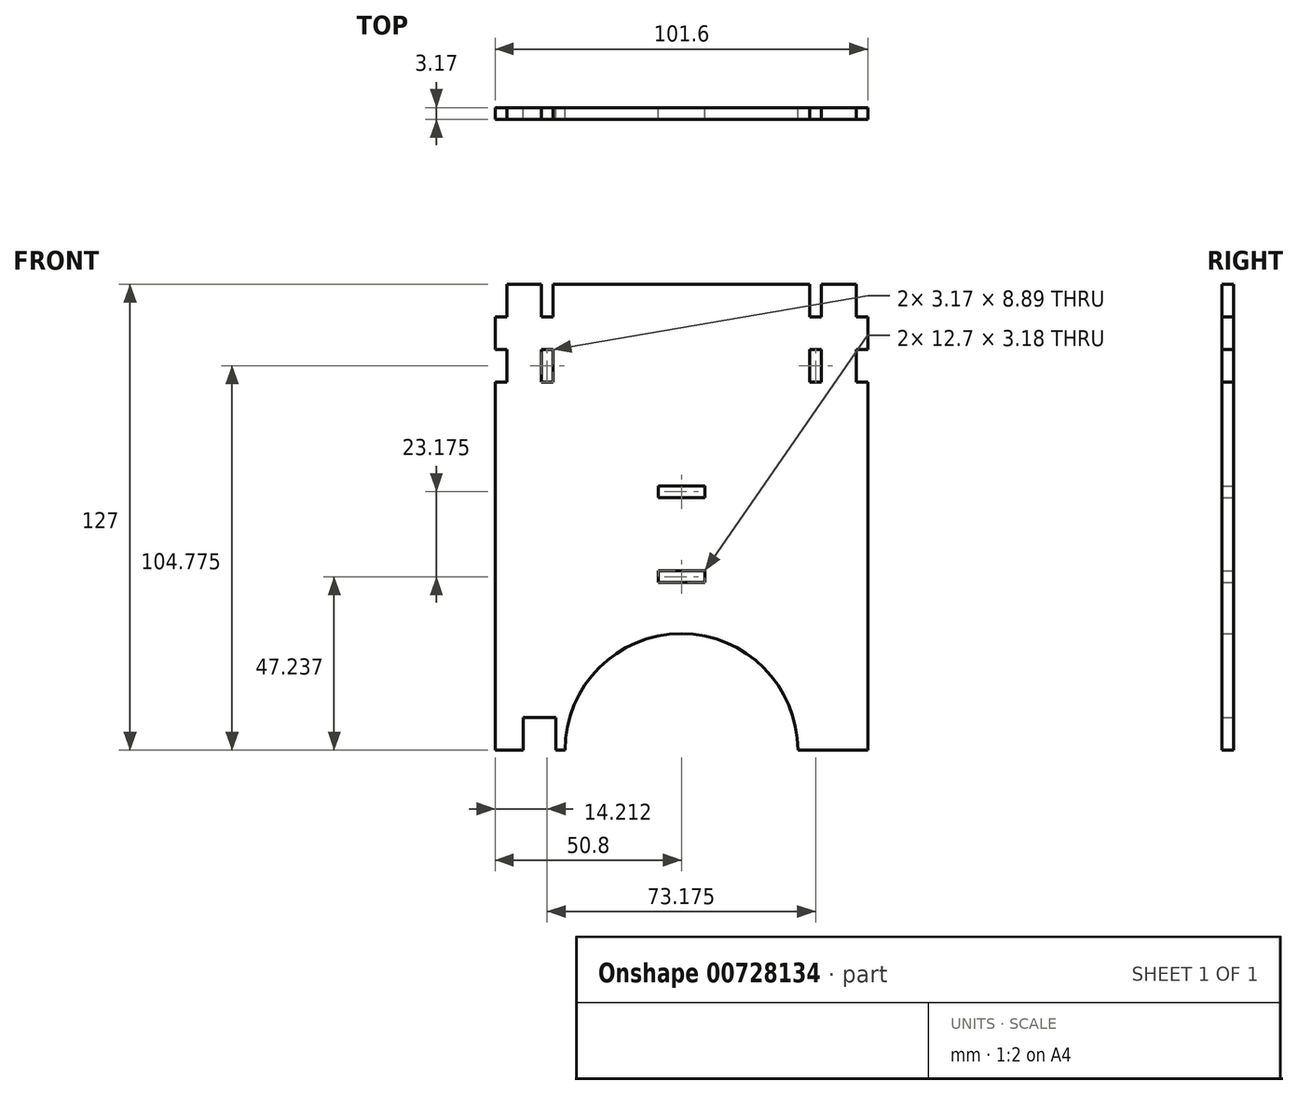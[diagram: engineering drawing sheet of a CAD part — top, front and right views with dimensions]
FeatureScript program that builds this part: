
annotation { "Feature Type Name" : "Feature", "Feature Type Description" : "" }
export const myFeature = defineFeature(function(context is Context, id is Id, definition is map)
    precondition{}
    {
        {
            var Q0;
            Q0=qCreatedBy(makeId("Front.planeOp"),FACE);
            var sketch = newSketch(context, id + "F0", { "sketchPlane" : qUnion([Q0])});
            skLineSegment(sketch, "E0.bottom", {"start": v(-50.8, 76.2) * mm, "end": v(50.8, 76.2) * mm});
            skLineSegment(sketch, "E0.top", {"start": v(-50.8, -76.2) * mm, "end": v(50.8, -76.2) * mm});
            skLineSegment(sketch, "E0.left", {"start": v(-50.8, 76.2) * mm, "end": v(-50.8, -76.2) * mm});
            skLineSegment(sketch, "E0.right", {"start": v(50.8, 76.2) * mm, "end": v(50.8, -76.2) * mm});
            skPoint(sketch, "E1", {"position": v(50.8, 0) * mm});
            skLineSegment(sketch, "E2", {"start": v(-47.62, 0) * mm, "end": v(-47.63, 76.2) * mm});
            skLineSegment(sketch, "E3", {"start": v(-50.8, 67.3) * mm, "end": v(-47.63, 67.3) * mm});
            skLineSegment(sketch, "E4", {"start": v(-50.8, 58.42) * mm, "end": v(-47.63, 58.42) * mm});
            skLineSegment(sketch, "E5", {"start": v(-50.8, 49.53) * mm, "end": v(-47.63, 49.53) * mm});
            skLineSegment(sketch, "E6", {"start": v(-50.8, 40.64) * mm, "end": v(-47.63, 40.64) * mm});
            skLineSegment(sketch, "E7", {"start": v(-50.8, 27.94) * mm, "end": v(-47.62, 27.94) * mm});
            skLineSegment(sketch, "E8", {"start": v(-47.62, 0) * mm, "end": v(-50.8, 0) * mm});
            skLineSegment(sketch, "E9", {"start": v(47.63, 76.2) * mm, "end": v(47.63, 0) * mm});
            skLineSegment(sketch, "E10", {"start": v(47.62, 67.31) * mm, "end": v(50.8, 67.31) * mm});
            skLineSegment(sketch, "E11", {"start": v(47.62, 58.42) * mm, "end": v(50.8, 58.42) * mm});
            skLineSegment(sketch, "E12", {"start": v(47.63, 38.1) * mm, "end": v(50.8, 38.1) * mm});
            skLineSegment(sketch, "E13", {"start": v(47.63, 25.4) * mm, "end": v(50.8, 25.4) * mm});
            skLineSegment(sketch, "E14", {"start": v(47.63, 12.7) * mm, "end": v(50.8, 12.7) * mm});
            skLineSegment(sketch, "E15", {"start": v(-35, 76.2) * mm, "end": v(-35, 0) * mm});
            skLineSegment(sketch, "E16", {"start": v(35, 76.2) * mm, "end": v(35, 0) * mm});
            skLineSegment(sketch, "E17", {"start": v(38.17, 0) * mm, "end": v(38.17, 76.2) * mm});
            skLineSegment(sketch, "E18", {"start": v(-38.18, 76.2) * mm, "end": v(-38.18, 0) * mm});
            skLineSegment(sketch, "E19", {"start": v(-38.17, 67.3) * mm, "end": v(-35, 67.3) * mm});
            skLineSegment(sketch, "E20", {"start": v(-35, -59.7) * mm, "end": v(-38.17, -59.7) * mm});
            skLineSegment(sketch, "E21", {"start": v(-35, -72.4) * mm, "end": v(-38.17, -72.4) * mm});
            skLineSegment(sketch, "E22", {"start": v(-38.17, -85.1) * mm, "end": v(-35, -85.1) * mm});
            skLineSegment(sketch, "E23", {"start": v(-35, -97.8) * mm, "end": v(-38.17, -97.8) * mm});
            skLineSegment(sketch, "E24", {"start": v(-38.18, 0) * mm, "end": v(-35, 0) * mm});
            skLineSegment(sketch, "E25", {"start": v(35, 0) * mm, "end": v(38.17, 0) * mm});
            skLineSegment(sketch, "E26", {"start": v(38.18, 27.94) * mm, "end": v(35, 27.94) * mm});
            skLineSegment(sketch, "E27", {"start": v(35, 40.64) * mm, "end": v(38.18, 40.64) * mm});
            skLineSegment(sketch, "E28", {"start": v(35, 49.53) * mm, "end": v(38.18, 49.53) * mm});
            skLineSegment(sketch, "E29", {"start": v(35, 58.42) * mm, "end": v(38.18, 58.42) * mm});
            skLineSegment(sketch, "E30", {"start": v(35, 67.31) * mm, "end": v(38.18, 67.31) * mm});
            skLineSegment(sketch, "E31", {"start": v(47.63, 0) * mm, "end": v(50.8, 0) * mm});
            skLineSegment(sketch, "E32.bottom", {"start": v(31.75, 21.2) * mm, "end": v(-31.75, 21.2) * mm});
            skLineSegment(sketch, "E32.top", {"start": v(31.75, 18.02) * mm, "end": v(-31.75, 18.02) * mm});
            skLineSegment(sketch, "E32.left", {"start": v(31.75, 21.2) * mm, "end": v(31.75, 18.02) * mm});
            skLineSegment(sketch, "E32.right", {"start": v(-31.75, 21.2) * mm, "end": v(-31.75, 18.02) * mm});
            skPoint(sketch, "E32.middle", {"position": v(0, 19.61) * mm});
            skLineSegment(sketch, "E33", {"start": v(-19.05, 21.2) * mm, "end": v(-19.05, 18.02) * mm});
            skLineSegment(sketch, "E34", {"start": v(-6.35, 21.2) * mm, "end": v(-6.35, 18.02) * mm});
            skLineSegment(sketch, "E35", {"start": v(6.35, 21.2) * mm, "end": v(6.35, 18.02) * mm});
            skLineSegment(sketch, "E36", {"start": v(19.05, 21.2) * mm, "end": v(19.05, 18.02) * mm});
            skLineSegment(sketch, "E37.bottom", {"start": v(31.75, -1.98) * mm, "end": v(-31.75, -1.98) * mm});
            skLineSegment(sketch, "E37.top", {"start": v(31.75, -5.15) * mm, "end": v(-31.75, -5.15) * mm});
            skLineSegment(sketch, "E37.left", {"start": v(31.75, -1.98) * mm, "end": v(31.75, -5.15) * mm});
            skLineSegment(sketch, "E37.right", {"start": v(-31.75, -1.98) * mm, "end": v(-31.75, -5.15) * mm});
            skPoint(sketch, "E37.middle", {"position": v(0, -3.56) * mm});
            skLineSegment(sketch, "E38", {"start": v(-19.05, -1.98) * mm, "end": v(-19.05, -5.15) * mm});
            skLineSegment(sketch, "E39", {"start": v(-6.35, -5.15) * mm, "end": v(-6.35, -1.98) * mm});
            skLineSegment(sketch, "E40", {"start": v(6.35, -1.98) * mm, "end": v(6.35, -5.15) * mm});
            skLineSegment(sketch, "E41", {"start": v(19.05, -5.15) * mm, "end": v(19.05, -1.98) * mm});
            skLineSegment(sketch, "E42", {"start": v(-50.8, -50.8) * mm, "end": v(50.8, -50.8) * mm});
            skLineSegment(sketch, "E43.bottom", {"start": v(-25.4, -50.8) * mm, "end": v(-16.5, -50.8) * mm});
            skLineSegment(sketch, "E43.top", {"start": v(-25.4, -41.9) * mm, "end": v(-16.51, -41.9) * mm});
            skLineSegment(sketch, "E43.left", {"start": v(-16.5, -50.8) * mm, "end": v(-16.51, -41.9) * mm});
            skLineSegment(sketch, "E43.right", {"start": v(-25.4, -50.8) * mm, "end": v(-25.4, -41.9) * mm});
            skLineSegment(sketch, "E44.bottom", {"start": v(16.51, -50.8) * mm, "end": v(25.4, -50.8) * mm});
            skLineSegment(sketch, "E44.top", {"start": v(16.51, -41.9) * mm, "end": v(25.4, -41.9) * mm});
            skLineSegment(sketch, "E44.left", {"start": v(25.4, -50.8) * mm, "end": v(25.4, -41.9) * mm});
            skLineSegment(sketch, "E44.right", {"start": v(16.51, -50.8) * mm, "end": v(16.51, -41.9) * mm});
            skLineSegment(sketch, "E45", {"start": v(-35, 58.42) * mm, "end": v(-38.17, 58.42) * mm});
            skLineSegment(sketch, "E46", {"start": v(-38.17, 49.53) * mm, "end": v(-35, 49.53) * mm});
            skLineSegment(sketch, "E47", {"start": v(47.62, 49.53) * mm, "end": v(50.8, 49.53) * mm});
            skLineSegment(sketch, "E48.bottom", {"start": v(-34.29, -50.8) * mm, "end": v(-43.18, -50.8) * mm});
            skLineSegment(sketch, "E48.top", {"start": v(-34.29, -41.9) * mm, "end": v(-43.18, -41.9) * mm});
            skLineSegment(sketch, "E48.left", {"start": v(-34.29, -50.8) * mm, "end": v(-34.29, -41.9) * mm});
            skLineSegment(sketch, "E48.right", {"start": v(-43.18, -50.8) * mm, "end": v(-43.18, -41.9) * mm});
            skArc(sketch, "E49", {"start": v(31.75, -50.8) * mm, "mid": v(0, -19.05) * mm, "end": v(-31.75, -50.8) * mm});
            skSolve(sketch);
        }
        {
            var Q0;
            {var subQ0=sQuery(id+"F0.wireOp",EDGE,"E3");Q0=makeQuery(id+"F0.imprint","IMPRINT",FACE,{"disambiguationData":[TD([[makeQuery(id+"F0.imprint","IMPRINT",EDGE,{"derivedFrom":subQ0}),-1.0]])]});}
            var Q1;
            {var subQ0=sQuery(id+"F0.wireOp",EDGE,"E5");Q1=makeQuery(id+"F0.imprint","IMPRINT",FACE,{"disambiguationData":[TD([[makeQuery(id+"F0.imprint","IMPRINT",EDGE,{"derivedFrom":subQ0}),-1.0]])]});}
            var Q2;
            {var subQ0=sQuery(id+"F0.wireOp",EDGE,"E7");Q2=makeQuery(id+"F0.imprint","IMPRINT",FACE,{"disambiguationData":[TD([[makeQuery(id+"F0.imprint","IMPRINT",EDGE,{"derivedFrom":subQ0}),-1.0]])]});}
            var Q3;
            {var subQ0=sQuery(id+"F0.wireOp",EDGE,"E12");Q3=makeQuery(id+"F0.imprint","IMPRINT",FACE,{"disambiguationData":[TD([[makeQuery(id+"F0.imprint","IMPRINT",EDGE,{"derivedFrom":subQ0}),-1.0]])]});}
            var Q4;
            {var subQ0=sQuery(id+"F0.wireOp",EDGE,"E10");Q4=makeQuery(id+"F0.imprint","IMPRINT",FACE,{"disambiguationData":[TD([[makeQuery(id+"F0.imprint","IMPRINT",EDGE,{"derivedFrom":subQ0}),-1.0]])]});}
            var Q5;
            {var subQ0=sQuery(id+"F0.wireOp",EDGE,"E21");Q5=makeQuery(id+"F0.imprint","IMPRINT",FACE,{"disambiguationData":[TD([[makeQuery(id+"F0.imprint","IMPRINT",EDGE,{"derivedFrom":subQ0}),1.0]])]});}
            var Q6;
            {var subQ2=sQuery(id+"F0.wireOp",EDGE,"E23");Q6=makeQuery(id+"F0.imprint","IMPRINT",FACE,{"disambiguationData":[TD([[makeQuery(id+"F0.imprint","IMPRINT",EDGE,{"derivedFrom":subQ2}),1.0]])]});}
            var Q7;
            {var subQ0=sQuery(id+"F0.wireOp",EDGE,"E25");Q7=makeQuery(id+"F0.imprint","IMPRINT",FACE,{"disambiguationData":[TD([[makeQuery(id+"F0.imprint","IMPRINT",EDGE,{"derivedFrom":subQ0}),1.0]])]});}
            var Q8;
            {var subQ0=sQuery(id+"F0.wireOp",EDGE,"E27");Q8=makeQuery(id+"F0.imprint","IMPRINT",FACE,{"disambiguationData":[TD([[makeQuery(id+"F0.imprint","IMPRINT",EDGE,{"derivedFrom":subQ0}),1.0]])]});}
            var Q9;
            {var subQ0=sQuery(id+"F0.wireOp",EDGE,"E29");Q9=makeQuery(id+"F0.imprint","IMPRINT",FACE,{"disambiguationData":[TD([[makeQuery(id+"F0.imprint","IMPRINT",EDGE,{"derivedFrom":subQ0}),1.0]])]});}
            var Q10;
            {var subQ0=sQuery(id+"F0.wireOp",EDGE,"E14");Q10=makeQuery(id+"F0.imprint","IMPRINT",FACE,{"disambiguationData":[TD([[makeQuery(id+"F0.imprint","IMPRINT",EDGE,{"derivedFrom":subQ0}),-1.0]])]});}
            var Q11;
            {var subQ0=sQuery(id+"F0.wireOp",EDGE,"E33");Q11=makeQuery(id+"F0.imprint","IMPRINT",FACE,{"disambiguationData":[TD([[makeQuery(id+"F0.imprint","IMPRINT",EDGE,{"derivedFrom":subQ0}),1.0]])]});}
            var Q12;
            {var subQ0=sQuery(id+"F0.wireOp",EDGE,"E35");Q12=makeQuery(id+"F0.imprint","IMPRINT",FACE,{"disambiguationData":[TD([[makeQuery(id+"F0.imprint","IMPRINT",EDGE,{"derivedFrom":subQ0}),1.0]])]});}
            var Q13;
            {var subQ0=sQuery(id+"F0.wireOp",EDGE,"E38");Q13=makeQuery(id+"F0.imprint","IMPRINT",FACE,{"disambiguationData":[TD([[makeQuery(id+"F0.imprint","IMPRINT",EDGE,{"derivedFrom":subQ0}),1.0]])]});}
            var Q14;
            {var subQ0=sQuery(id+"F0.wireOp",EDGE,"E40");Q14=makeQuery(id+"F0.imprint","IMPRINT",FACE,{"disambiguationData":[TD([[makeQuery(id+"F0.imprint","IMPRINT",EDGE,{"derivedFrom":subQ0}),1.0]])]});}
            var Q15;
            {var subQ51=sQuery(id+"F0.wireOp",EDGE,"E8");Q15=makeQuery(id+"F0.imprint","IMPRINT",FACE,{"disambiguationData":[TD([[makeQuery(id+"F0.imprint","IMPRINT",EDGE,{"derivedFrom":subQ51}),1.0]])]});}
            var Q16;
            {var subQ0=sQuery(id+"F0.wireOp",EDGE,"E6");Q16=makeQuery(id+"F0.imprint","IMPRINT",FACE,{"disambiguationData":[TD([[makeQuery(id+"F0.imprint","IMPRINT",EDGE,{"derivedFrom":subQ0}),-1.0]])]});}
            var Q17;
            {var subQ0=sQuery(id+"F0.wireOp",EDGE,"E13");Q17=makeQuery(id+"F0.imprint","IMPRINT",FACE,{"disambiguationData":[TD([[makeQuery(id+"F0.imprint","IMPRINT",EDGE,{"derivedFrom":subQ0}),-1.0]])]});}
            var Q18;
            {var subQ0=sQuery(id+"F0.wireOp",EDGE,"E26");Q18=makeQuery(id+"F0.imprint","IMPRINT",FACE,{"disambiguationData":[TD([[makeQuery(id+"F0.imprint","IMPRINT",EDGE,{"derivedFrom":subQ0}),-1.0]])]});}
            var Q19;
            {var subQ0=sQuery(id+"F0.wireOp",EDGE,"E22");Q19=makeQuery(id+"F0.imprint","IMPRINT",FACE,{"disambiguationData":[TD([[makeQuery(id+"F0.imprint","IMPRINT",EDGE,{"derivedFrom":subQ0}),-1.0]])]});}
            var Q20;
            {var subQ0=sQuery(id+"F0.wireOp",EDGE,"E32.right");Q20=makeQuery(id+"F0.imprint","IMPRINT",FACE,{"disambiguationData":[TD([[makeQuery(id+"F0.imprint","IMPRINT",EDGE,{"derivedFrom":subQ0}),1.0]])]});}
            var Q21;
            {var subQ0=sQuery(id+"F0.wireOp",EDGE,"E32.left");Q21=makeQuery(id+"F0.imprint","IMPRINT",FACE,{"disambiguationData":[TD([[makeQuery(id+"F0.imprint","IMPRINT",EDGE,{"derivedFrom":subQ0}),-1.0]])]});}
            var Q22;
            {var subQ0=sQuery(id+"F0.wireOp",EDGE,"E37.left");Q22=makeQuery(id+"F0.imprint","IMPRINT",FACE,{"disambiguationData":[TD([[makeQuery(id+"F0.imprint","IMPRINT",EDGE,{"derivedFrom":subQ0}),-1.0]])]});}
            var Q23;
            {var subQ0=sQuery(id+"F0.wireOp",EDGE,"E37.right");Q23=makeQuery(id+"F0.imprint","IMPRINT",FACE,{"disambiguationData":[TD([[makeQuery(id+"F0.imprint","IMPRINT",EDGE,{"derivedFrom":subQ0}),1.0]])]});}
            var Q24;
            {var subQ2=sQuery(id+"F0.wireOp",EDGE,"E19");Q24=makeQuery(id+"F0.imprint","IMPRINT",FACE,{"disambiguationData":[TD([[makeQuery(id+"F0.imprint","IMPRINT",EDGE,{"derivedFrom":subQ2}),-1.0]])]});}
            var Q25;
            {var subQ0=sQuery(id+"F0.wireOp",EDGE,"E24");Q25=makeQuery(id+"F0.imprint","IMPRINT",FACE,{"disambiguationData":[TD([[makeQuery(id+"F0.imprint","IMPRINT",EDGE,{"derivedFrom":subQ0}),1.0]])]});}
            var Q26;
            {var subQ0=sQuery(id+"F0.wireOp",EDGE,"E12");Q26=makeQuery(id+"F0.imprint","IMPRINT",FACE,{"disambiguationData":[TD([[makeQuery(id+"F0.imprint","IMPRINT",EDGE,{"derivedFrom":subQ0}),1.0]])]});}
            var Q27;
            Q27=makeQuery(id+"F0.imprint","IMPRINT",FACE,{"disambiguationData":[TD([[makeQuery(id+"F0.imprint","IMPRINT",EDGE,{"derivedFrom":sQuery(id+"F0.wireOp",EDGE,"E48.bottom")}),-1.0]])]});
            extrude(context, id + "F1", {"entities" : qUnion([Q0, Q1, Q2, Q3, Q4, Q5, Q6, Q7, Q8, Q9, Q10, Q11, Q12, Q13, Q14, Q15, Q16, Q17, Q18, Q19, Q20, Q21, Q22, Q23, Q24, Q25, Q26, Q27]), "depth" : 3.17 * mm, "offsetDistance" : 25.4 * mm});
        }
    });
